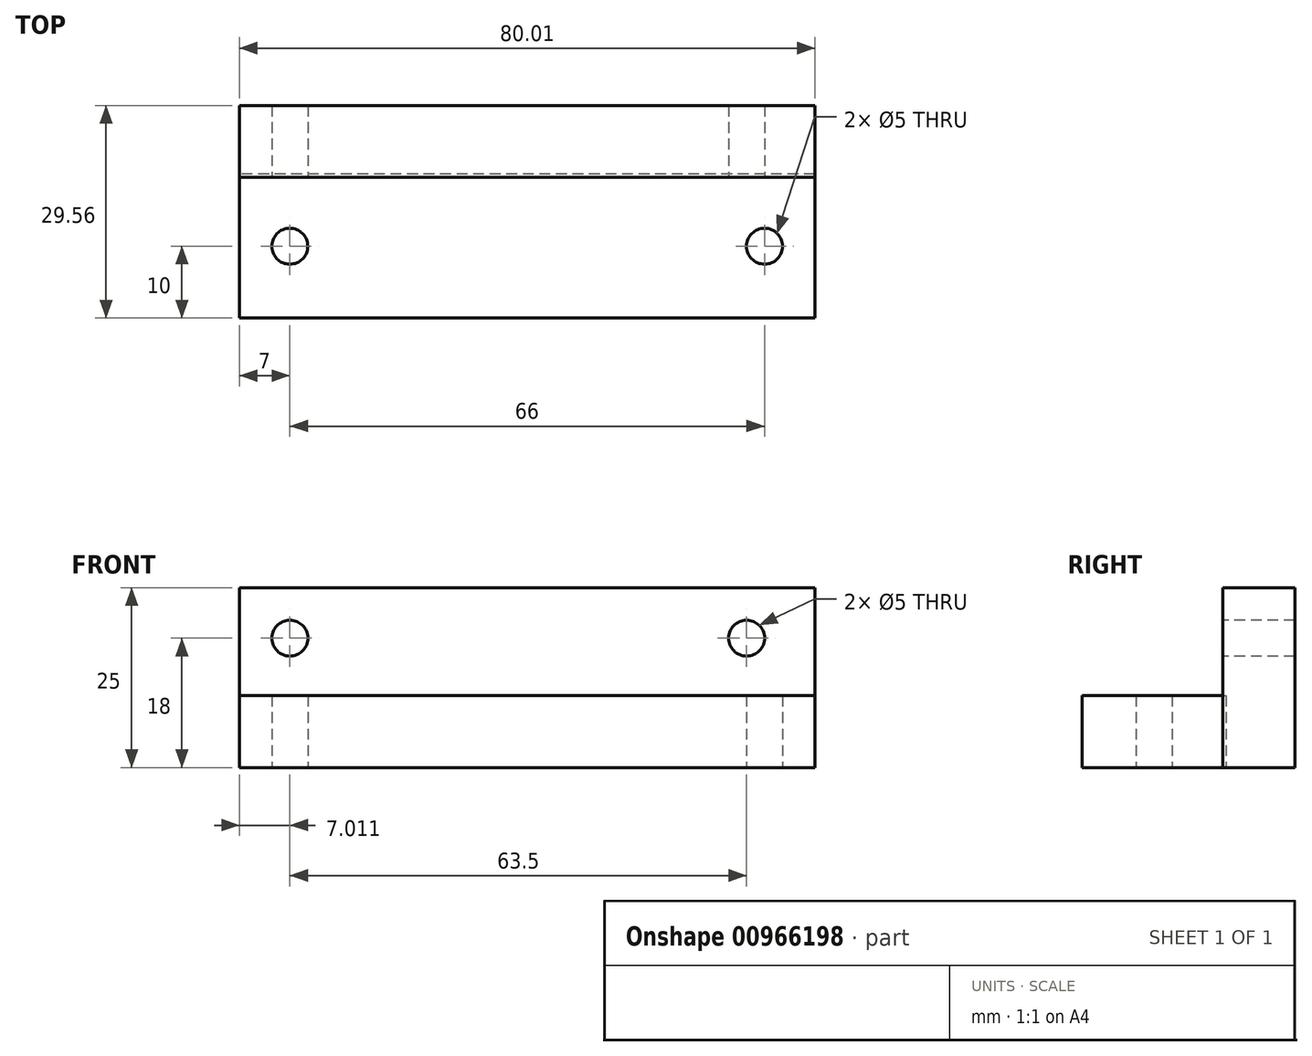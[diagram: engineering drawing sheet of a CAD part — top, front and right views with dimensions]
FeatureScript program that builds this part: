
annotation { "Feature Type Name" : "Feature", "Feature Type Description" : "" }
export const myFeature = defineFeature(function(context is Context, id is Id, definition is map)
    precondition{}
    {
        {
            var Q0;
            Q0=qCreatedBy(makeId("Top.planeOp"),FACE);
            var sketch = newSketch(context, id + "F0", { "sketchPlane" : qUnion([Q0])});
            skLineSegment(sketch, "E0.bottom", {"start": v(40, -10) * mm, "end": v(-40, -10) * mm});
            skLineSegment(sketch, "E0.top", {"start": v(40, 10) * mm, "end": v(-40, 10) * mm});
            skLineSegment(sketch, "E0.left", {"start": v(40, -10) * mm, "end": v(40, 10) * mm});
            skLineSegment(sketch, "E0.right", {"start": v(-40, -10) * mm, "end": v(-40, 10) * mm});
            skPoint(sketch, "E0.middle", {"position": v(0, 0) * mm});
            skCircle(sketch, "E1", {"center": v(33, 0) * mm, "radius": 2.5 * mm});
            skCircle(sketch, "E2", {"center": v(-33, 0) * mm, "radius": 2.5 * mm});
            skSolve(sketch);
        }
        {
            var Q0;
            Q0=makeQuery(id+"F0.imprint","IMPRINT",FACE,{"disambiguationData":[TD([[makeQuery(id+"F0.imprint","IMPRINT",EDGE,{"derivedFrom":sQuery(id+"F0.wireOp",EDGE,"E0.bottom")}),-1.0]])]});
            extrude(context, id + "F1", {"entities" : qUnion([Q0]), "depth" : 10 * mm, "offsetDistance" : 25 * mm});
        }
        {
            var Q0;
            Q0=qCreatedBy(makeId("Top.planeOp"),FACE);
            var sketch = newSketch(context, id + "F2", { "sketchPlane" : qUnion([Q0])});
            skLineSegment(sketch, "E3.bottom", {"start": v(-39.99, 10.06) * mm, "end": v(40.01, 10.06) * mm});
            skLineSegment(sketch, "E3.top", {"start": v(-39.99, 20.06) * mm, "end": v(40.01, 20.06) * mm});
            skLineSegment(sketch, "E3.left", {"start": v(-39.99, 10.06) * mm, "end": v(-39.99, 20.06) * mm});
            skLineSegment(sketch, "E3.right", {"start": v(40.01, 10.06) * mm, "end": v(40.01, 20.06) * mm});
            skSolve(sketch);
        }
        {
            var Q0;
            Q0=makeQuery(id+"F2.imprint","IMPRINT",FACE,{"disambiguationData":[TD([[makeQuery(id+"F2.imprint","IMPRINT",EDGE,{"derivedFrom":sQuery(id+"F2.wireOp",EDGE,"E3.bottom")}),1.0]])]});
            extrude(context, id + "F3", {"entities" : qUnion([Q0]), "depth" : 25 * mm, "offsetDistance" : 25 * mm});
        }
        {
            var Q0;
            Q0=makeQuery(id+"F3.opExtrude","SWEPT_FACE",FACE,{"disambiguationData":[OSD([sQuery(id+"F2.wireOp",EDGE,"E3.bottom")])]});
            var sketch = newSketch(context, id + "F4", { "sketchPlane" : qUnion([Q0])});
            skCircle(sketch, "E4", {"center": v(-32.99, 18) * mm, "radius": 2.5 * mm});
            skCircle(sketch, "E5", {"center": v(30.51, 18) * mm, "radius": 2.5 * mm});
            skSolve(sketch);
        }
        {
            var Q0;
            Q0=makeQuery(id+"F4.imprint","IMPRINT",FACE,{"disambiguationData":[TD([[makeQuery(id+"F4.imprint","IMPRINT",EDGE,{"derivedFrom":sQuery(id+"F4.wireOp",EDGE,"E4")}),1.0]])]});
            var Q1;
            Q1=makeQuery(id+"F4.imprint","IMPRINT",FACE,{"disambiguationData":[TD([[makeQuery(id+"F4.imprint","IMPRINT",EDGE,{"derivedFrom":sQuery(id+"F4.wireOp",EDGE,"E5")}),1.0]])]});
            extrude(context, id + "F5", {"entities" : qUnion([Q0, Q1]), "operationType" : NewBodyOperationType.REMOVE, "oppositeDirection" : true, "depth" : 14.8 * mm, "offsetDistance" : 25 * mm});
        }
        {
            var Q0;
            Q0=makeQuery(id+"F3.opExtrude","SWEPT_BODY",BODY,{"disambiguationData":[OSD([sQuery(id+"F2.wireOp",EDGE,"E3.bottom"),sQuery(id+"F2.wireOp",EDGE,"E3.top"),sQuery(id+"F2.wireOp",EDGE,"E3.left"),sQuery(id+"F2.wireOp",EDGE,"E3.right")])]});
            transform(context, id + "F6", {"entities" : qUnion([Q0]), "transformType" : TransformType.TRANSLATION_3D, "dx" : 0 * mm, "dy" : -0.5 * mm, "dz" : 0 * mm, "makeCopy" : false});
        }
    });
